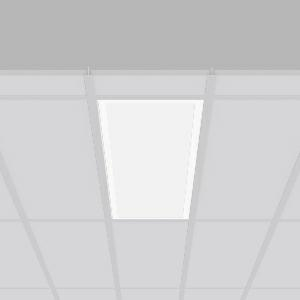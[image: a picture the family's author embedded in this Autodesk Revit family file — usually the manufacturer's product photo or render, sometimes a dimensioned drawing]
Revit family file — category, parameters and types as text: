
# Revit family: sidelite_eco_672378_002_1_04_4def
name_source: partatom
category: Lighting Fixtures
units: mm (PartAtom-declared; Revit-internal decimal feet)

## family parameters
Cut with Voids When Loaded = No
Host = Face
Light Source = No
Part Type = Normal
Room Calculation Point = No
Round Connector Dimension = Use Diameter
Shared = No

## types (1)
- SIDELITE ECO (1 x LED Modul 840, 3500 lm, 4000)
    Apparent Load = 29 VA
    CIE Flux Codes = 47 79 96 100 100
    Color Rendering = 80
    Color Temperature = 4000
    Default Elevation = 1800 mm
    Description = Series: SIDELITE ECO
Highly economical recessed luminaire with progressive LED technology. For escape route illumination. Frame made of aluminium, powder-coated. Diffuser: plastic, opal. Lightguide and diffuser made of non-yellowing plastic (PMMA). Lateral light emission (RZB SIDELITE technology) for homogeneous light distribution. External driver. Self-contained system with automatic self-test and feedback to the RZB monitoring system MULTIDIGIT. External driver with simple plug-in locking system. Extended connection cable (1.90 m). 
Colour: white
Length: 1245 mm
Width: 308 mm
Cut-out length: 1220 mm
Cut-out width: 285 mm
Recess height: 160 mm
Luminaire: recess height: 40 mm
Weight: 4.7 kg
Operating mode: maintained power mode
Duration time: 8 h
Lamp: LED
Socket: without socket
Colour temperature: 4000K
Colour rendering index (CRI): 80
System power: 29 W
Rated luminous flux: 3500 lm
Luminous flux, emergency: 240 lm
System power, emergency: -
Control gear: Regulated power supply
Protection class: I
Type of protection: IP 40
    Height = 0 mm  [stored 0 ft]
    Lamp = 1 x LED Modul 840
    Lamp Light Flux = 3500 lm
    Lamp count = 1
    Length = 1245 mm
    Lifetime = 50000 h
    Luminous efficacy = 121 lm/W
    Manufacturer = RZB
    ModVariant = No
    Model = 672378.002.1.04
    Mounting Place = Ceiling
    Mounting Type = Recessed
    Number of Poles = 1
    OnlyDefault = Yes
    Power Factor = 1
    Product Name = SIDELITE ECO
    Product group = Recessed modular luminaires
    ProductGroupID = 406
    Protection Class = Protection class I
    Protection Degree = IP 40
    RLX_Detail_Level = 1
    RLX_Emergency_Light_Flux = 240 lm
    RLX_Emergency_Type = 3
    RLX_Emergency_Type_DB = Yes
    RlxData = <blob elided: 30053 chars, md5=0e97c4af>
    Socket = socket
    Standby Power = 0 W
    System Light Flux = 3500 lm
    System Power = 29 W
    Type Comments = Product without accessories
    Type Image = 312367.002.jpg
    URL = http://relux.com
    VarID = ---
    Voltage = 230 V
    Voltage Range = 220-240 V
    Weight = 0.00 kg
    Width = 308 mm

note: [stored X ft] marks values corroborated as IEEE doubles in the binary element streams (Revit-internal decimal feet)

## geometry (parser evidence)
native form markers: Blend x4, Sweep x10
no freeform markers — native parametric forms only
